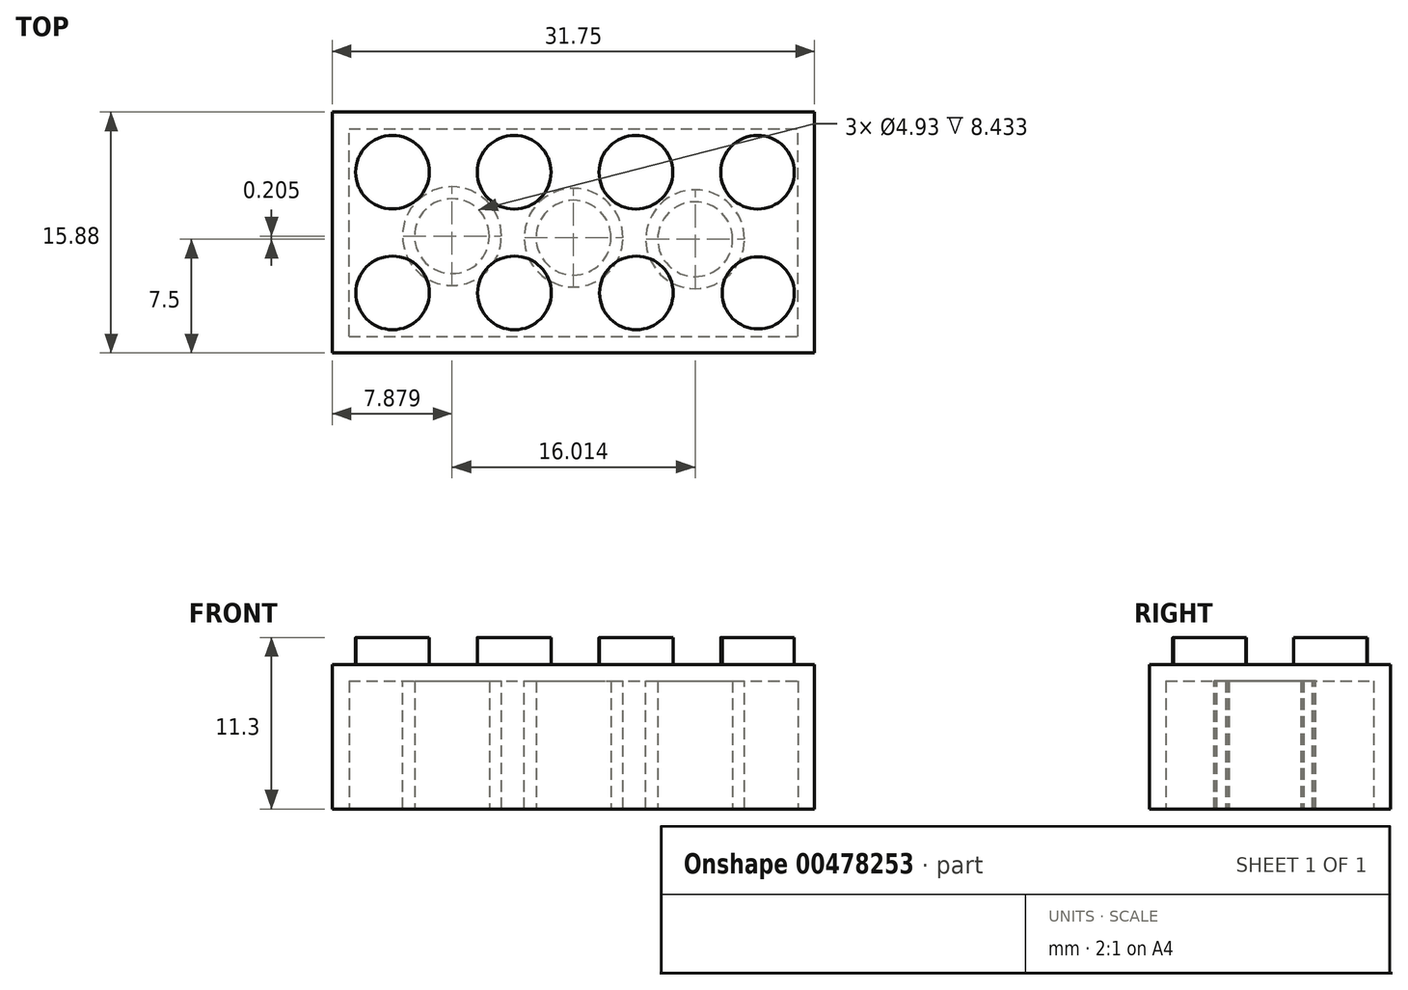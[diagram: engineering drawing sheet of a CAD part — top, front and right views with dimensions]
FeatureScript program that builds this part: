
annotation { "Feature Type Name" : "Feature", "Feature Type Description" : "" }
export const myFeature = defineFeature(function(context is Context, id is Id, definition is map)
    precondition{}
    {
        {
            var Q0;
            Q0=qCreatedBy(makeId("Top.planeOp"),FACE);
            var sketch = newSketch(context, id + "F0", { "sketchPlane" : qUnion([Q0])});
            skLineSegment(sketch, "E0.bottom", {"start": v(-46.78, 32) * mm, "end": v(-15.03, 32) * mm});
            skLineSegment(sketch, "E0.top", {"start": v(-46.78, 16.13) * mm, "end": v(-15.03, 16.13) * mm});
            skLineSegment(sketch, "E0.left", {"start": v(-46.78, 32) * mm, "end": v(-46.78, 16.13) * mm});
            skLineSegment(sketch, "E0.right", {"start": v(-15.03, 32) * mm, "end": v(-15.03, 16.13) * mm});
            skSolve(sketch);
        }
        {
            var Q0;
            Q0=makeQuery(id+"F0.imprint","IMPRINT",FACE,{"disambiguationData":[TD([[makeQuery(id+"F0.imprint","IMPRINT",EDGE,{"derivedFrom":sQuery(id+"F0.wireOp",EDGE,"E0.bottom")}),-1.0]])]});
            extrude(context, id + "F1", {"entities" : qUnion([Q0]), "depth" : 9.52 * mm, "offsetDistance" : 25.4 * mm});
        }
        {
            var Q0;
            Q0=makeQuery(id+"F1.opExtrude","CAP_FACE",FACE,{"disambiguationData":[OSD([sQuery(id+"F0.wireOp",EDGE,"E0.bottom"),sQuery(id+"F0.wireOp",EDGE,"E0.top"),sQuery(id+"F0.wireOp",EDGE,"E0.left"),sQuery(id+"F0.wireOp",EDGE,"E0.right")])],"isStart":false});
            var sketch = newSketch(context, id + "F2", { "sketchPlane" : qUnion([Q0])});
            skCircle(sketch, "E1", {"center": v(-42.82, 28.05) * mm, "radius": 2.43 * mm});
            skSolve(sketch);
        }
        {
            var Q0;
            Q0=makeQuery(id+"F1.opExtrude","CAP_FACE",FACE,{"disambiguationData":[OSD([sQuery(id+"F0.wireOp",EDGE,"E0.bottom"),sQuery(id+"F0.wireOp",EDGE,"E0.top"),sQuery(id+"F0.wireOp",EDGE,"E0.left"),sQuery(id+"F0.wireOp",EDGE,"E0.right")])],"isStart":false});
            var sketch = newSketch(context, id + "F3", { "sketchPlane" : qUnion([Q0])});
            skCircle(sketch, "E2", {"center": v(-34.8, 28.04) * mm, "radius": 2.43 * mm});
            skSolve(sketch);
        }
        {
            var Q0;
            Q0=makeQuery(id+"F2.imprint","IMPRINT",FACE,{"disambiguationData":[TD([[makeQuery(id+"F2.imprint","IMPRINT",EDGE,{"derivedFrom":sQuery(id+"F2.wireOp",EDGE,"E1")}),-1.0]])]});
            var sketch = newSketch(context, id + "F4", { "sketchPlane" : qUnion([Q0])});
            skCircle(sketch, "E3", {"center": v(-26.8, 28.04) * mm, "radius": 2.43 * mm});
            skSolve(sketch);
        }
        {
            var Q0;
            Q0=makeQuery(id+"F2.imprint","IMPRINT",FACE,{"disambiguationData":[TD([[makeQuery(id+"F2.imprint","IMPRINT",EDGE,{"derivedFrom":sQuery(id+"F2.wireOp",EDGE,"E1")}),-1.0]])]});
            var sketch = newSketch(context, id + "F5", { "sketchPlane" : qUnion([Q0])});
            skCircle(sketch, "E4", {"center": v(-18.78, 28.04) * mm, "radius": 2.43 * mm});
            skSolve(sketch);
        }
        {
            var Q0;
            Q0=makeQuery(id+"F3.imprint","IMPRINT",FACE,{"disambiguationData":[TD([[makeQuery(id+"F3.imprint","IMPRINT",EDGE,{"derivedFrom":sQuery(id+"F3.wireOp",EDGE,"E2")}),-1.0]])]});
            var sketch = newSketch(context, id + "F6", { "sketchPlane" : qUnion([Q0])});
            skCircle(sketch, "E5", {"center": v(-42.81, 20.1) * mm, "radius": 2.43 * mm});
            skSolve(sketch);
        }
        {
            var Q0;
            Q0=makeQuery(id+"F2.imprint","IMPRINT",FACE,{"disambiguationData":[TD([[makeQuery(id+"F2.imprint","IMPRINT",EDGE,{"derivedFrom":sQuery(id+"F2.wireOp",EDGE,"E1")}),-1.0]])]});
            var sketch = newSketch(context, id + "F7", { "sketchPlane" : qUnion([Q0])});
            skCircle(sketch, "E6", {"center": v(-34.79, 20.1) * mm, "radius": 2.43 * mm});
            skSolve(sketch);
        }
        {
            var Q0;
            Q0=makeQuery(id+"F2.imprint","IMPRINT",FACE,{"disambiguationData":[TD([[makeQuery(id+"F2.imprint","IMPRINT",EDGE,{"derivedFrom":sQuery(id+"F2.wireOp",EDGE,"E1")}),-1.0]])]});
            var sketch = newSketch(context, id + "F8", { "sketchPlane" : qUnion([Q0])});
            skCircle(sketch, "E7", {"center": v(-26.76, 20.1) * mm, "radius": 2.43 * mm});
            skSolve(sketch);
        }
        {
            var Q0;
            Q0=makeQuery(id+"F6.imprint","IMPRINT",FACE,{"disambiguationData":[TD([[makeQuery(id+"F6.imprint","IMPRINT",EDGE,{"derivedFrom":sQuery(id+"F6.wireOp",EDGE,"E5")}),-1.0]])]});
            var sketch = newSketch(context, id + "F9", { "sketchPlane" : qUnion([Q0])});
            skCircle(sketch, "E8", {"center": v(-18.73, 20.1) * mm, "radius": 2.38 * mm});
            skSolve(sketch);
        }
        {
            var Q0;
            Q0 = qSketchRegion(id + "F2", true);
            extrude(context, id + "F10", {"entities" : qUnion([Q0]), "operationType" : NewBodyOperationType.ADD, "depth" : 1.78 * mm});
        }
        {
            var Q0;
            Q0 = qSketchRegion(id + "F3", true);
            extrude(context, id + "F11", {"entities" : qUnion([Q0]), "operationType" : NewBodyOperationType.ADD, "depth" : 1.78 * mm});
        }
        {
            var Q0;
            Q0 = qSketchRegion(id + "F4", true);
            extrude(context, id + "F12", {"entities" : qUnion([Q0]), "operationType" : NewBodyOperationType.ADD, "depth" : 1.78 * mm});
        }
        {
            var Q0;
            Q0 = qSketchRegion(id + "F5", true);
            extrude(context, id + "F13", {"entities" : qUnion([Q0]), "operationType" : NewBodyOperationType.ADD, "depth" : 1.78 * mm});
        }
        {
            var Q0;
            Q0 = qSketchRegion(id + "F6", true);
            extrude(context, id + "F14", {"entities" : qUnion([Q0]), "operationType" : NewBodyOperationType.ADD, "depth" : 1.78 * mm});
        }
        {
            var Q0;
            Q0 = qSketchRegion(id + "F7", true);
            extrude(context, id + "F15", {"entities" : qUnion([Q0]), "operationType" : NewBodyOperationType.ADD, "depth" : 1.78 * mm});
        }
        {
            var Q0;
            Q0 = qSketchRegion(id + "F8", true);
            extrude(context, id + "F16", {"entities" : qUnion([Q0]), "operationType" : NewBodyOperationType.ADD, "depth" : 1.78 * mm});
        }
        {
            var Q0;
            Q0 = qSketchRegion(id + "F9", true);
            extrude(context, id + "F17", {"entities" : qUnion([Q0]), "operationType" : NewBodyOperationType.ADD, "depth" : 1.78 * mm});
        }
        {
            var Q0;
            Q0=makeQuery(id+"F1.opExtrude","CAP_FACE",FACE,{"disambiguationData":[OSD([sQuery(id+"F0.wireOp",EDGE,"E0.bottom"),sQuery(id+"F0.wireOp",EDGE,"E0.top"),sQuery(id+"F0.wireOp",EDGE,"E0.left"),sQuery(id+"F0.wireOp",EDGE,"E0.right")])],"isStart":true});
            var sketch = newSketch(context, id + "F18", { "sketchPlane" : qUnion([Q0])});
            skLineSegment(sketch, "E9.bottom", {"start": v(-45.68, -17.22) * mm, "end": v(-16.12, -17.22) * mm});
            skLineSegment(sketch, "E9.top", {"start": v(-45.68, -30.91) * mm, "end": v(-16.12, -30.91) * mm});
            skLineSegment(sketch, "E9.left", {"start": v(-45.68, -17.22) * mm, "end": v(-45.68, -30.91) * mm});
            skLineSegment(sketch, "E9.right", {"start": v(-16.12, -17.22) * mm, "end": v(-16.12, -30.91) * mm});
            skSolve(sketch);
        }
        {
            var Q0;
            Q0 = qSketchRegion(id + "F18", true);
            extrude(context, id + "F19", {"entities" : qUnion([Q0]), "operationType" : NewBodyOperationType.REMOVE, "oppositeDirection" : true, "depth" : 8.43 * mm, "offsetDistance" : 25.4 * mm});
        }
        {
            var Q0;
            Q0=makeQuery(id+"F19.boolean.opBoolean","COPY",FACE,{"derivedFrom":makeQuery(id+"F19.opExtrude","CAP_FACE",FACE,{"disambiguationData":[OSD([sQuery(id+"F18.wireOp",EDGE,"E9.bottom"),sQuery(id+"F18.wireOp",EDGE,"E9.top"),sQuery(id+"F18.wireOp",EDGE,"E9.left"),sQuery(id+"F18.wireOp",EDGE,"E9.right")])],"isStart":false})});
            var sketch = newSketch(context, id + "F20", { "sketchPlane" : qUnion([Q0])});
            skCircle(sketch, "E10", {"center": v(-38.9, -23.83) * mm, "radius": 3.25 * mm});
            skCircle(sketch, "E11", {"center": v(-30.9, -23.73) * mm, "radius": 3.25 * mm});
            skCircle(sketch, "E12", {"center": v(-22.89, -23.63) * mm, "radius": 3.25 * mm});
            skSolve(sketch);
        }
        {
            var Q0;
            Q0 = qSketchRegion(id + "F20", true);
            extrude(context, id + "F21", {"entities" : qUnion([Q0]), "operationType" : NewBodyOperationType.ADD, "depth" : 8.43 * mm, "offsetDistance" : 25.4 * mm});
        }
        {
            var Q0;
            Q0=makeQuery(id+"F21.opExtrude","CAP_FACE",FACE,{"disambiguationData":[OSD([sQuery(id+"F20.wireOp",EDGE,"E10")])],"isStart":false});
            var sketch = newSketch(context, id + "F22", { "sketchPlane" : qUnion([Q0])});
            skCircle(sketch, "E13", {"center": v(-38.9, -23.83) * mm, "radius": 2.46 * mm});
            skCircle(sketch, "E14", {"center": v(-30.9, -23.73) * mm, "radius": 2.46 * mm});
            skCircle(sketch, "E15", {"center": v(-22.89, -23.63) * mm, "radius": 2.46 * mm});
            skSolve(sketch);
        }
        {
            var Q0;
            Q0 = qSketchRegion(id + "F22", true);
            extrude(context, id + "F23", {"entities" : qUnion([Q0]), "operationType" : NewBodyOperationType.REMOVE, "oppositeDirection" : true, "depth" : 8.43 * mm, "offsetDistance" : 25.4 * mm});
        }
    });
